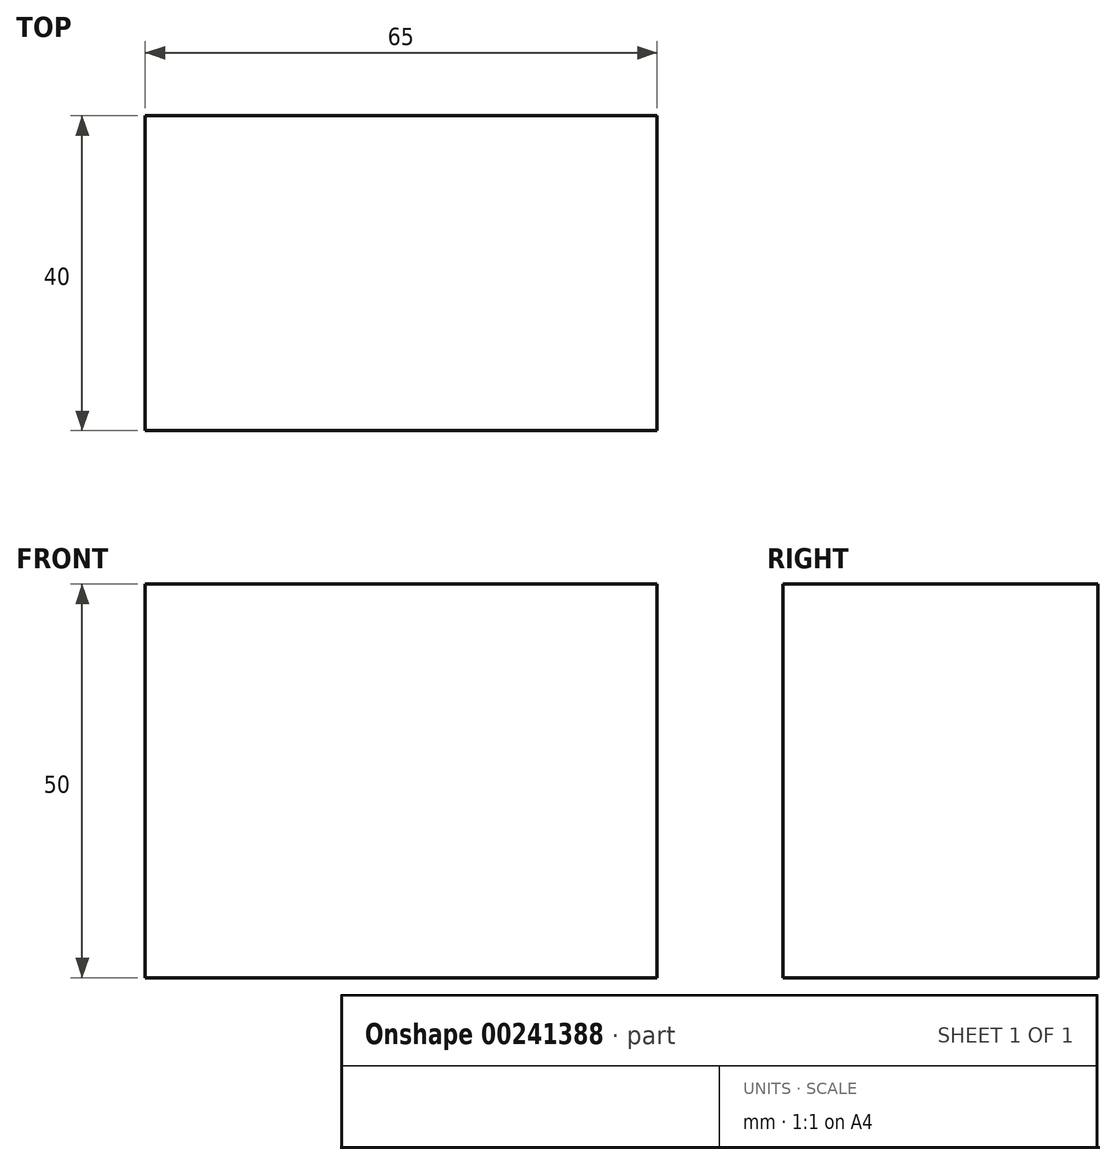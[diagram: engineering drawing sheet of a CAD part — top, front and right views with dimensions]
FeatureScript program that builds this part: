
annotation { "Feature Type Name" : "Feature", "Feature Type Description" : "" }
export const myFeature = defineFeature(function(context is Context, id is Id, definition is map)
    precondition{}
    {
        {
            var Q0;
            Q0=qCreatedBy(makeId("Right.planeOp"),FACE);
            var sketch = newSketch(context, id + "F0", { "sketchPlane" : qUnion([Q0])});
            skLineSegment(sketch, "E0.bottom", {"start": v(-20, 25) * mm, "end": v(20, 25) * mm});
            skLineSegment(sketch, "E0.top", {"start": v(-20, -25) * mm, "end": v(20, -25) * mm});
            skLineSegment(sketch, "E0.left", {"start": v(-20, 25) * mm, "end": v(-20, -25) * mm});
            skLineSegment(sketch, "E0.right", {"start": v(20, 25) * mm, "end": v(20, -25) * mm});
            skPoint(sketch, "E0.middle", {"position": v(0, 0) * mm});
            skSolve(sketch);
        }
        {
            var Q0;
            Q0 = qSketchRegion(id + "F0", true);
            extrude(context, id + "F1", {"entities" : qUnion([Q0]), "depth" : 65 * mm});
        }
    });
